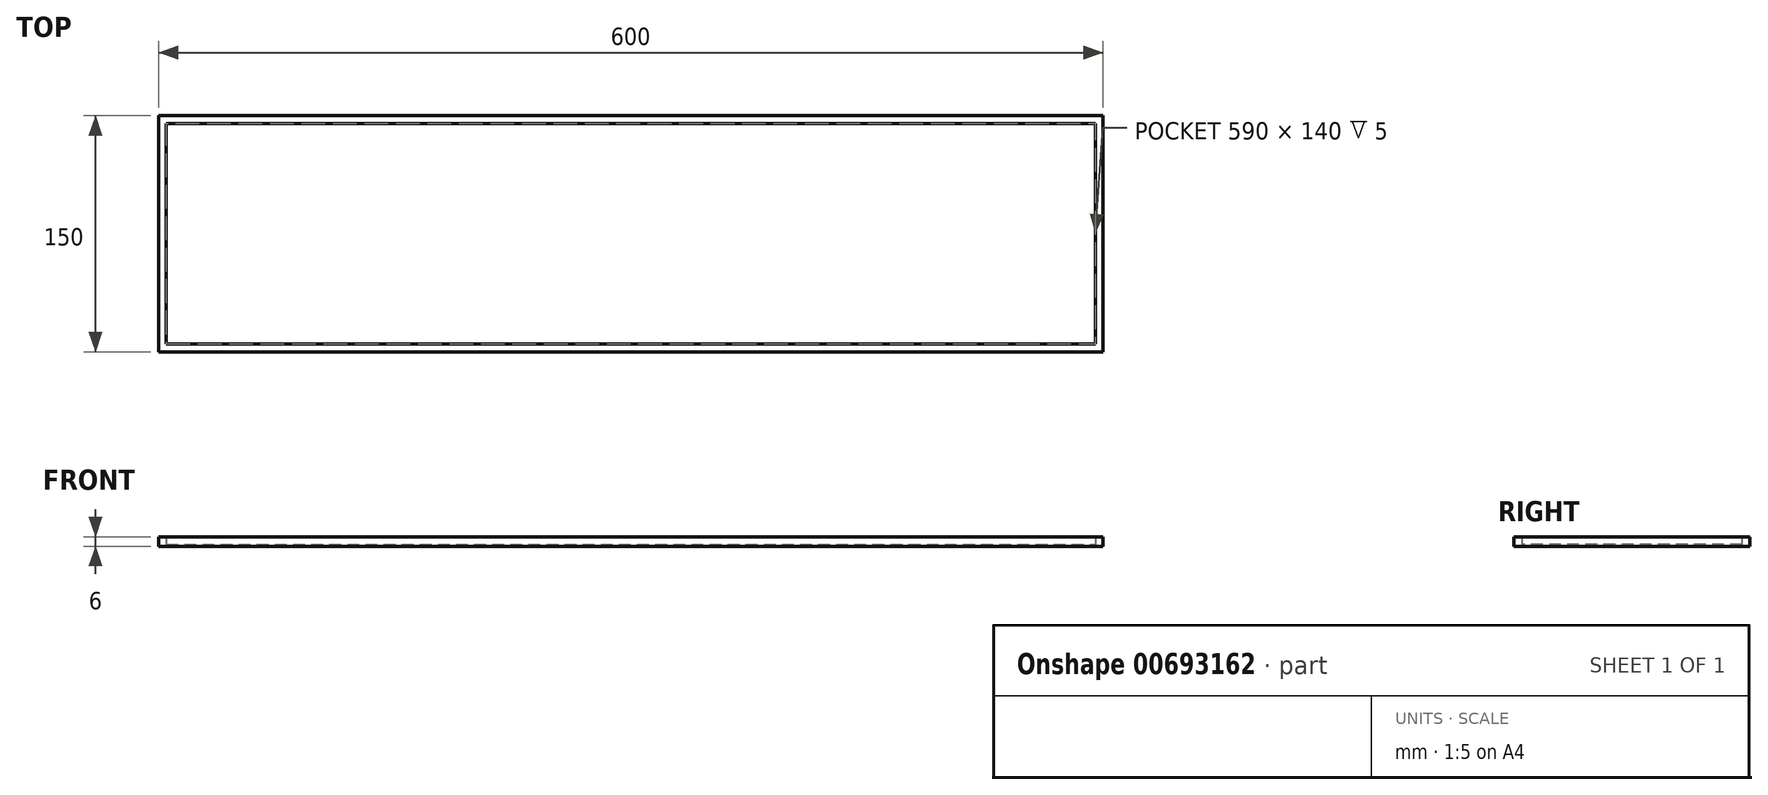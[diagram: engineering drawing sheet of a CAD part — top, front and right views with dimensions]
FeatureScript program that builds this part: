
annotation { "Feature Type Name" : "Feature", "Feature Type Description" : "" }
export const myFeature = defineFeature(function(context is Context, id is Id, definition is map)
    precondition{}
    {
        {
            var Q0;
            Q0=qCreatedBy(makeId("Top.planeOp"),FACE);
            var sketch = newSketch(context, id + "F0", { "sketchPlane" : qUnion([Q0])});
            skLineSegment(sketch, "E0.bottom", {"start": v(-288.8, 31.74) * mm, "end": v(311.2, 31.74) * mm});
            skLineSegment(sketch, "E0.top", {"start": v(-288.8, -118.26) * mm, "end": v(311.2, -118.26) * mm});
            skLineSegment(sketch, "E0.left", {"start": v(-288.8, 31.74) * mm, "end": v(-288.8, -118.26) * mm});
            skLineSegment(sketch, "E0.right", {"start": v(311.2, 31.74) * mm, "end": v(311.2, -118.26) * mm});
            skLineSegment(sketch, "E1.direction1", {"start": v(300.03, 11.74) * mm, "end": v(325.03, 11.74) * mm, "construction": true});
            skLineSegment(sketch, "E2.bottom", {"start": v(-283.8, 26.74) * mm, "end": v(306.2, 26.74) * mm});
            skLineSegment(sketch, "E2.top", {"start": v(-283.8, -113.26) * mm, "end": v(306.2, -113.26) * mm});
            skLineSegment(sketch, "E2.left", {"start": v(-283.8, 26.74) * mm, "end": v(-283.8, -113.26) * mm});
            skLineSegment(sketch, "E2.right", {"start": v(306.2, 26.74) * mm, "end": v(306.2, -113.26) * mm});
            skSolve(sketch);
        }
        {
            var Q0;
            Q0=qSketchRegion(id+"F0",true);
            extrude(context, id + "F1", {"entities" : qUnion([Q0]), "depth" : 5 * mm, "offsetDistance" : 25 * mm});
        }
        {
            var Q0;
            Q0=makeQuery(id+"F1.opExtrude","CAP_FACE",FACE,{"disambiguationData":[OSD([sQuery(id+"F0.wireOp",EDGE,"E0.bottom"),sQuery(id+"F0.wireOp",EDGE,"E0.top"),sQuery(id+"F0.wireOp",EDGE,"E0.left"),sQuery(id+"F0.wireOp",EDGE,"E0.right"),sQuery(id+"F0.wireOp",EDGE,"Q3saARHD-Gs58-2NVK-PtzY-fhxvJSEAU8xS.bottom"),sQuery(id+"F0.wireOp",EDGE,"Q3saARHD-Gs58-2NVK-PtzY-fhxvJSEAU8xS.top"),sQuery(id+"F0.wireOp",EDGE,"Q3saARHD-Gs58-2NVK-PtzY-fhxvJSEAU8xS.left"),sQuery(id+"F0.wireOp",EDGE,"Q3saARHD-Gs58-2NVK-PtzY-fhxvJSEAU8xS.right"),sQuery(id+"F0.wireOp",EDGE,"E1.0.1.0"),sQuery(id+"F0.wireOp",EDGE,"E1.0.1.1"),sQuery(id+"F0.wireOp",EDGE,"E1.0.1.2"),sQuery(id+"F0.wireOp",EDGE,"E1.0.1.3"),sQuery(id+"F0.wireOp",EDGE,"E1.0.2.0"),sQuery(id+"F0.wireOp",EDGE,"E1.0.2.1"),sQuery(id+"F0.wireOp",EDGE,"E1.0.2.2"),sQuery(id+"F0.wireOp",EDGE,"E1.0.2.3"),sQuery(id+"F0.wireOp",EDGE,"E1.0.3.0"),sQuery(id+"F0.wireOp",EDGE,"E1.0.3.1"),sQuery(id+"F0.wireOp",EDGE,"E1.0.3.2"),sQuery(id+"F0.wireOp",EDGE,"E1.0.3.3"),sQuery(id+"F0.wireOp",EDGE,"E1.0.4.0"),sQuery(id+"F0.wireOp",EDGE,"E1.0.4.1"),sQuery(id+"F0.wireOp",EDGE,"E1.0.4.2"),sQuery(id+"F0.wireOp",EDGE,"E1.0.4.3"),sQuery(id+"F0.wireOp",EDGE,"E1.0.5.0"),sQuery(id+"F0.wireOp",EDGE,"E1.0.5.1"),sQuery(id+"F0.wireOp",EDGE,"E1.0.5.2"),sQuery(id+"F0.wireOp",EDGE,"E1.0.5.3"),sQuery(id+"F0.wireOp",EDGE,"E1.0.6.0"),sQuery(id+"F0.wireOp",EDGE,"E1.0.6.1"),sQuery(id+"F0.wireOp",EDGE,"E1.0.6.2"),sQuery(id+"F0.wireOp",EDGE,"E1.0.6.3")])],"isStart":true});
            var sketch = newSketch(context, id + "F2", { "sketchPlane" : qUnion([Q0])});
            skLineSegment(sketch, "E3.bottom", {"start": v(-288.8, -31.74) * mm, "end": v(311.2, -31.74) * mm});
            skLineSegment(sketch, "E3.top", {"start": v(-288.8, 118.26) * mm, "end": v(311.2, 118.26) * mm});
            skLineSegment(sketch, "E3.left", {"start": v(-288.8, -31.74) * mm, "end": v(-288.8, 118.26) * mm});
            skLineSegment(sketch, "E3.right", {"start": v(311.2, -31.74) * mm, "end": v(311.2, 118.26) * mm});
            skSolve(sketch);
        }
        {
            var Q0;
            Q0=qSketchRegion(id+"F2",true);
            extrude(context, id + "F3", {"entities" : qUnion([Q0]), "operationType" : NewBodyOperationType.ADD, "depth" : 1 * mm, "offsetDistance" : 25 * mm});
        }
        {
            var Q0;
            Q0 = qSketchRegion(id + "F0", true);
            extrude(context, id + "F4", {"entities" : qUnion([Q0]), "operationType" : NewBodyOperationType.ADD, "depth" : 1 * mm, "offsetDistance" : 25 * mm});
        }
    });
